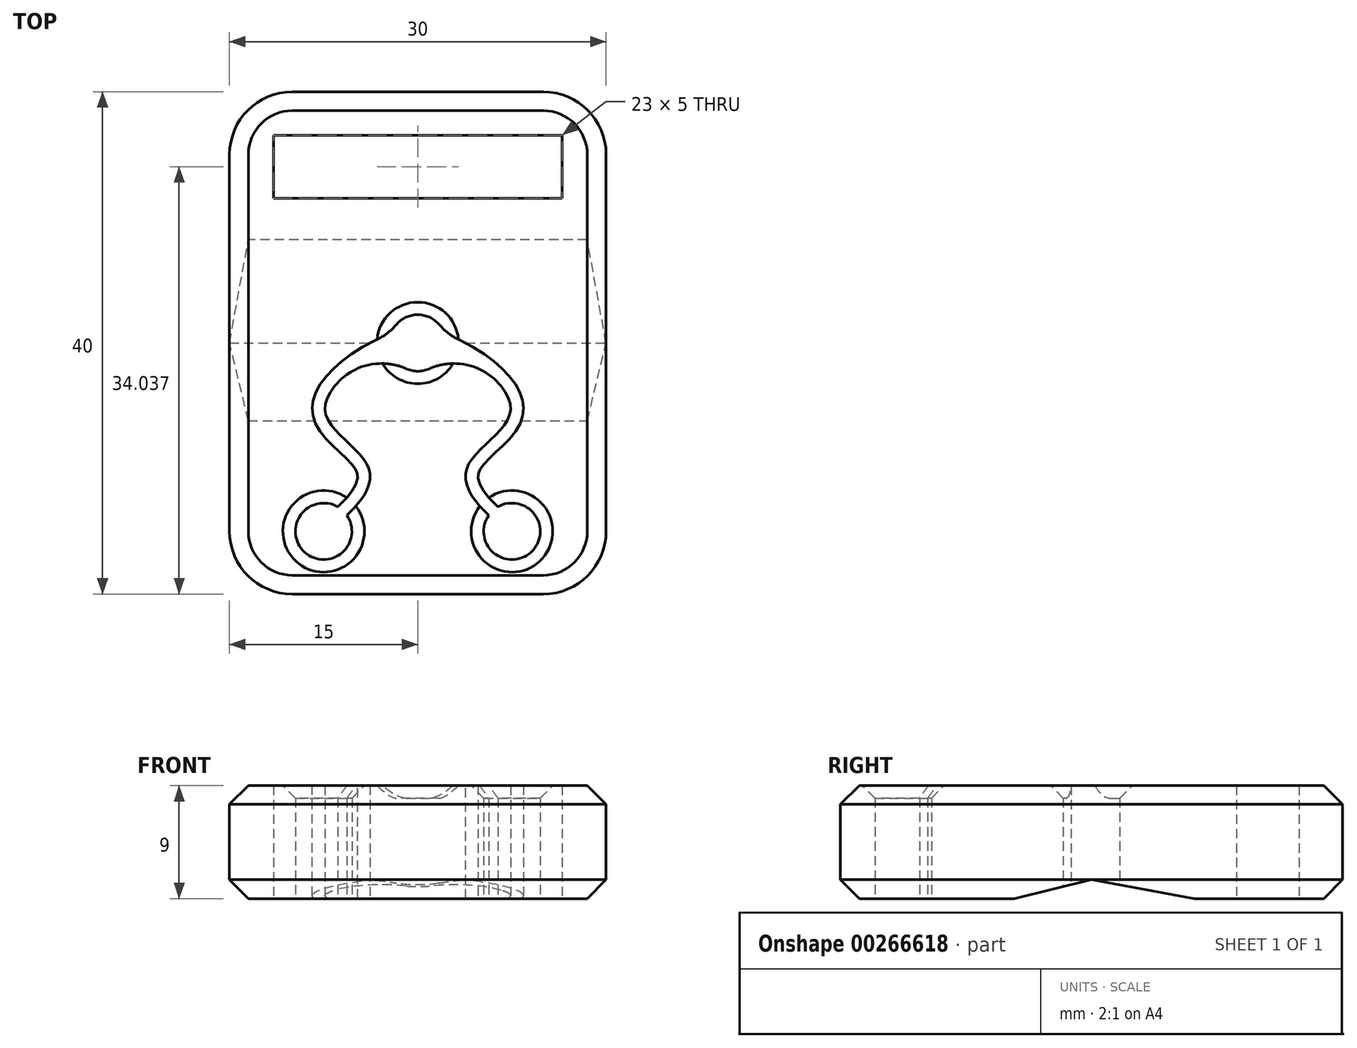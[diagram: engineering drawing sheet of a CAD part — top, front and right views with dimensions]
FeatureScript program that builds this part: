
annotation { "Feature Type Name" : "Feature", "Feature Type Description" : "" }
export const myFeature = defineFeature(function(context is Context, id is Id, definition is map)
    precondition{}
    {
        {
            var Q0;
            Q0=qCreatedBy(makeId("Top.planeOp"),FACE);
            var sketch = newSketch(context, id + "F0", { "sketchPlane" : qUnion([Q0])});
            skLineSegment(sketch, "E0.bottom", {"start": v(15, -20) * mm, "end": v(-15, -20) * mm});
            skLineSegment(sketch, "E0.top", {"start": v(15, 20) * mm, "end": v(-15, 20) * mm});
            skLineSegment(sketch, "E0.left", {"start": v(15, -20) * mm, "end": v(15, 20) * mm});
            skLineSegment(sketch, "E0.right", {"start": v(-15, -20) * mm, "end": v(-15, 20) * mm});
            skPoint(sketch, "E0.middle", {"position": v(0, 0) * mm});
            skSolve(sketch);
        }
        {
            var Q0;
            Q0 = qSketchRegion(id + "F0", true);
            extrude(context, id + "F1", {"entities" : qUnion([Q0]), "endBound" : BoundingType.SYMMETRIC, "depth" : 9 * mm});
        }
        {
            var Q0;
            Q0=makeQuery(id+"F1.opExtrude","CAP_FACE",FACE,{"disambiguationData":[OSD([sQuery(id+"F0.wireOp",EDGE,"E0.bottom"),sQuery(id+"F0.wireOp",EDGE,"E0.top"),sQuery(id+"F0.wireOp",EDGE,"E0.left"),sQuery(id+"F0.wireOp",EDGE,"E0.right")])],"isStart":true});
            var sketch = newSketch(context, id + "F2", { "sketchPlane" : qUnion([Q0])});
            skLineSegment(sketch, "E1.bottom", {"start": v(11.5, -16.54) * mm, "end": v(-11.5, -16.54) * mm});
            skLineSegment(sketch, "E1.top", {"start": v(11.5, -11.54) * mm, "end": v(-11.5, -11.54) * mm});
            skLineSegment(sketch, "E1.left", {"start": v(11.5, -16.54) * mm, "end": v(11.5, -11.54) * mm});
            skLineSegment(sketch, "E1.right", {"start": v(-11.5, -16.54) * mm, "end": v(-11.5, -11.54) * mm});
            skPoint(sketch, "E1.middle", {"position": v(0, -14.04) * mm});
            skCircle(sketch, "E2", {"center": v(0, 0) * mm, "radius": 2.25 * mm});
            skCircle(sketch, "E3", {"center": v(-7.5, 15) * mm, "radius": 2.25 * mm});
            skCircle(sketch, "E4", {"center": v(7.5, 15) * mm, "radius": 2.25 * mm});
            skFitSpline(sketch, "E5", {"points": [v(-7.5, 15) * mm, v(-3.87, 10.1) * mm, v(-7.4, 5.22) * mm, v(0, 0) * mm], "startDerivative": vector(19.54, -10.83) * mm, "endDerivative": vector(22.53, 0) * mm});
            skLineSegment(sketch, "E6", {"start": v(0, 17.76) * mm, "end": v(0, -14.04) * mm, "construction": true});
            skFitSpline(sketch, "E7.MirrorCS", {"points": [v(7.5, 15) * mm, v(3.87, 10.1) * mm, v(7.4, 5.22) * mm, v(0, 0) * mm], "startDerivative": vector(-19.54, -10.83) * mm, "endDerivative": vector(-22.53, 0) * mm});
            skFitSpline(sketch, "E8.0", {"points": [v(7.98, 14.13) * mm, v(7.62, 13.92) * mm, v(6.87, 13.44) * mm, v(6.03, 12.72) * mm, v(5.5, 12.12) * mm, v(5.17, 11.68) * mm, v(4.94, 11.26) * mm, v(4.82, 10.9) * mm, v(4.8, 10.65) * mm, v(4.8, 10.48) * mm, v(4.83, 10.36) * mm, v(4.88, 10.23) * mm, v(4.98, 10.03) * mm, v(5.2, 9.72) * mm, v(5.58, 9.31) * mm, v(6.04, 8.87) * mm, v(6.55, 8.4) * mm, v(7.06, 7.9) * mm, v(7.56, 7.34) * mm, v(8, 6.72) * mm, v(8.27, 6.1) * mm, v(8.39, 5.55) * mm, v(8.4, 5.1) * mm, v(8.35, 4.66) * mm, v(8.2, 4.11) * mm, v(7.9, 3.47) * mm, v(7.39, 2.76) * mm, v(6.77, 2.1) * mm, v(6.07, 1.47) * mm, v(5.03, 0.7) * mm, v(3.59, -0.12) * mm, v(1.78, -0.8) * mm, v(0.58, -1) * mm, v(0, -1) * mm]});
            skFitSpline(sketch, "E8.1", {"points": [v(-7.98, 14.13) * mm, v(-7.62, 13.92) * mm, v(-6.87, 13.44) * mm, v(-6.03, 12.72) * mm, v(-5.5, 12.12) * mm, v(-5.17, 11.68) * mm, v(-4.94, 11.26) * mm, v(-4.82, 10.9) * mm, v(-4.8, 10.65) * mm, v(-4.8, 10.48) * mm, v(-4.83, 10.36) * mm, v(-4.88, 10.23) * mm, v(-4.98, 10.03) * mm, v(-5.2, 9.72) * mm, v(-5.58, 9.31) * mm, v(-6.04, 8.87) * mm, v(-6.55, 8.4) * mm, v(-7.06, 7.9) * mm, v(-7.56, 7.34) * mm, v(-8, 6.72) * mm, v(-8.27, 6.1) * mm, v(-8.39, 5.55) * mm, v(-8.4, 5.1) * mm, v(-8.35, 4.66) * mm, v(-8.2, 4.11) * mm, v(-7.9, 3.47) * mm, v(-7.39, 2.76) * mm, v(-6.77, 2.1) * mm, v(-6.07, 1.47) * mm, v(-5.03, 0.7) * mm, v(-3.59, -0.12) * mm, v(-1.78, -0.8) * mm, v(-0.58, -1) * mm, v(0, -1) * mm]});
            skLineSegment(sketch, "E9", {"start": v(-7.98, 14.13) * mm, "end": v(-7.5, 15) * mm});
            skLineSegment(sketch, "E10", {"start": v(7.5, 15) * mm, "end": v(7.98, 14.13) * mm});
            skSolve(sketch);
        }
        {
            var Q0;
            Q0 = qSketchRegion(id + "F2", true);
            extrude(context, id + "F3", {"entities" : qUnion([Q0]), "operationType" : NewBodyOperationType.REMOVE, "oppositeDirection" : true, "depth" : 25 * mm});
        }
        {
            var Q0;
            Q0=makeQuery(id+"F1.opExtrude","SWEPT_EDGE",EDGE,{"disambiguationData":[OSD([sQuery(id+"F0.wireOp",EDGE,"E0.bottom"),sQuery(id+"F0.wireOp",EDGE,"E0.right")])]});
            var Q1;
            Q1=makeQuery(id+"F1.opExtrude","SWEPT_EDGE",EDGE,{"disambiguationData":[OSD([sQuery(id+"F0.wireOp",EDGE,"E0.bottom"),sQuery(id+"F0.wireOp",EDGE,"E0.left")])]});
            var Q2;
            Q2=makeQuery(id+"F1.opExtrude","SWEPT_EDGE",EDGE,{"disambiguationData":[OSD([sQuery(id+"F0.wireOp",EDGE,"E0.top"),sQuery(id+"F0.wireOp",EDGE,"E0.right")])]});
            var Q3;
            Q3=makeQuery(id+"F1.opExtrude","SWEPT_EDGE",EDGE,{"disambiguationData":[OSD([sQuery(id+"F0.wireOp",EDGE,"E0.top"),sQuery(id+"F0.wireOp",EDGE,"E0.left")])]});
            fillet(context, id + "F4", {"entities" : qUnion([Q0, Q1, Q2, Q3]), "radius" : 5 * mm, "tangentPropagation" : true, "allowEdgeOverflow" : false});
        }
        {
            var Q0;
            Q0=makeQuery(id+"F1.opExtrude","CAP_EDGE",EDGE,{"disambiguationData":[OSD([sQuery(id+"F0.wireOp",EDGE,"E0.left")])],"isStart":true});
            var Q1;
            Q1=makeQuery(id+"F1.opExtrude","CAP_EDGE",EDGE,{"disambiguationData":[OSD([sQuery(id+"F0.wireOp",EDGE,"E0.left")])],"isStart":false});
            chamfer(context, id + "F5", {"entities" : qUnion([Q0, Q1]), "width" : 1.5 * mm, "tangentPropagation" : true});
        }
        {
            var Q0;
            Q0=makeQuery(id+"F1.opExtrude","SWEPT_FACE",FACE,{"disambiguationData":[OSD([sQuery(id+"F0.wireOp",EDGE,"E0.left")])]});
            var sketch = newSketch(context, id + "F6", { "sketchPlane" : qUnion([Q0])});
            skLineSegment(sketch, "E11", {"start": v(0, -3) * mm, "end": v(-11.3, -5.74) * mm});
            skLineSegment(sketch, "E12", {"start": v(-11.3, -5.74) * mm, "end": v(15, -5.74) * mm});
            skLineSegment(sketch, "E13", {"start": v(15, -5.74) * mm, "end": v(0, -3) * mm});
            skSolve(sketch);
        }
        {
            var Q0;
            Q0 = qSketchRegion(id + "F6", true);
            extrude(context, id + "F7", {"entities" : qUnion([Q0]), "operationType" : NewBodyOperationType.REMOVE, "oppositeDirection" : true, "depth" : 33 * mm});
        }
        {
            var Q0;
            Q0=makeQuery(id+"F3.boolean.opBoolean","COPY",EDGE,{"derivedFrom":makeQuery(id+"F3.opExtrude","CAP_EDGE",EDGE,{"disambiguationData":[OSD([sQuery(id+"F2.wireOp",EDGE,"E3")])],"isStart":true})});
            var Q1;
            Q1=makeQuery(id+"F3.boolean.opBoolean","COPY",EDGE,{"derivedFrom":makeQuery(id+"F3.opExtrude","CAP_EDGE",EDGE,{"disambiguationData":[OSD([sQuery(id+"F2.wireOp",EDGE,"E2")])],"isStart":true})});
            var Q2;
            Q2=makeQuery(id+"F3.boolean.opBoolean","COPY",EDGE,{"derivedFrom":makeQuery(id+"F3.opExtrude","CAP_EDGE",EDGE,{"disambiguationData":[OSD([sQuery(id+"F2.wireOp",EDGE,"E4")])],"isStart":true})});
            var Q3;
            Q3=makeQuery(id+"F3.boolean.opBoolean","INTERSECT",EDGE,{"derivedFrom":[makeQuery(id+"F1.opExtrude","CAP_FACE",FACE,{"disambiguationData":[OSD([sQuery(id+"F0.wireOp",EDGE,"E0.bottom"),sQuery(id+"F0.wireOp",EDGE,"E0.top"),sQuery(id+"F0.wireOp",EDGE,"E0.left"),sQuery(id+"F0.wireOp",EDGE,"E0.right")])],"isStart":false}),makeQuery(id+"F3.opExtrude","SWEPT_FACE",FACE,{"disambiguationData":[OSD([sQuery(id+"F2.wireOp",EDGE,"E3")])]})]});
            var Q4;
            Q4=makeQuery(id+"F3.boolean.opBoolean","INTERSECT",EDGE,{"derivedFrom":[makeQuery(id+"F1.opExtrude","CAP_FACE",FACE,{"disambiguationData":[OSD([sQuery(id+"F0.wireOp",EDGE,"E0.bottom"),sQuery(id+"F0.wireOp",EDGE,"E0.top"),sQuery(id+"F0.wireOp",EDGE,"E0.left"),sQuery(id+"F0.wireOp",EDGE,"E0.right")])],"isStart":false}),makeQuery(id+"F3.opExtrude","SWEPT_FACE",FACE,{"disambiguationData":[OSD([sQuery(id+"F2.wireOp",EDGE,"E2")])]})]});
            var Q5;
            Q5=makeQuery(id+"F3.boolean.opBoolean","INTERSECT",EDGE,{"derivedFrom":[makeQuery(id+"F1.opExtrude","CAP_FACE",FACE,{"disambiguationData":[OSD([sQuery(id+"F0.wireOp",EDGE,"E0.bottom"),sQuery(id+"F0.wireOp",EDGE,"E0.top"),sQuery(id+"F0.wireOp",EDGE,"E0.left"),sQuery(id+"F0.wireOp",EDGE,"E0.right")])],"isStart":false}),makeQuery(id+"F3.opExtrude","SWEPT_FACE",FACE,{"disambiguationData":[OSD([sQuery(id+"F2.wireOp",EDGE,"E4")])]})]});
            chamfer(context, id + "F8", {"entities" : qUnion([Q0, Q1, Q2, Q3, Q4, Q5]), "width" : 1 * mm, "tangentPropagation" : true});
        }
        {
            var Q0;
            Q0=makeQuery(id+"F3.boolean.opBoolean","COPY",EDGE,{"derivedFrom":makeQuery(id+"F3.opExtrude","SWEPT_EDGE",EDGE,{"disambiguationData":[OSD([sQuery(id+"F2.wireOp",EDGE,"E2"),sQuery(id+"F2.wireOp",EDGE,"E5")])]})});
            var Q1;
            Q1=makeQuery(id+"F3.boolean.opBoolean","COPY",EDGE,{"derivedFrom":makeQuery(id+"F3.opExtrude","SWEPT_EDGE",EDGE,{"disambiguationData":[OSD([sQuery(id+"F2.wireOp",EDGE,"E2"),sQuery(id+"F2.wireOp",EDGE,"E7.MirrorCS")])]})});
            var Q2;
            Q2=makeQuery(id+"F3.boolean.opBoolean","COPY",EDGE,{"derivedFrom":makeQuery(id+"F3.opExtrude","SWEPT_EDGE",EDGE,{"disambiguationData":[OSD([sQuery(id+"F2.wireOp",EDGE,"E2"),sQuery(id+"F2.wireOp",EDGE,"E8.1")])]})});
            var Q3;
            Q3=makeQuery(id+"F3.boolean.opBoolean","COPY",EDGE,{"derivedFrom":makeQuery(id+"F3.opExtrude","SWEPT_EDGE",EDGE,{"disambiguationData":[OSD([sQuery(id+"F2.wireOp",EDGE,"E2"),sQuery(id+"F2.wireOp",EDGE,"E8.0")])]})});
            fillet(context, id + "F9", {"entities" : qUnion([Q0, Q1, Q2, Q3]), "radius" : 4.8 * mm, "tangentPropagation" : true, "allowEdgeOverflow" : false});
        }
    });
